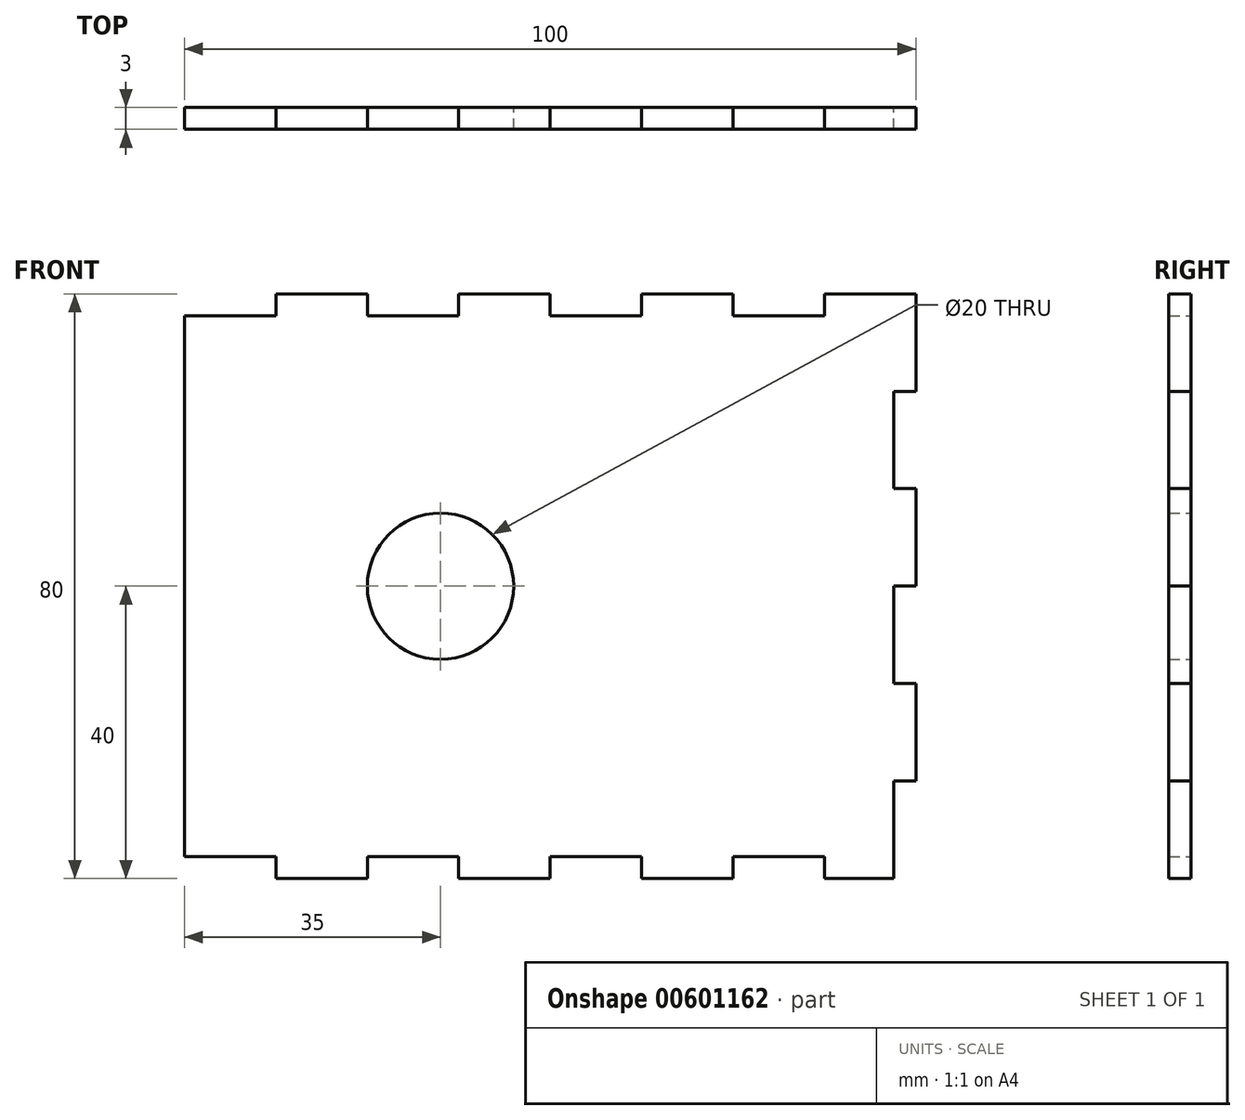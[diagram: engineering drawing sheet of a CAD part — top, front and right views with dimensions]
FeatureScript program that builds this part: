
annotation { "Feature Type Name" : "Feature", "Feature Type Description" : "" }
export const myFeature = defineFeature(function(context is Context, id is Id, definition is map)
    precondition{}
    {
        {
            var Q0;
            Q0=qCreatedBy(makeId("Front.planeOp"),FACE);
            var sketch = newSketch(context, id + "F0", { "sketchPlane" : qUnion([Q0])});
            skLineSegment(sketch, "E0.bottom", {"start": v(47, -40) * mm, "end": v(37.5, -40) * mm});
            skLineSegment(sketch, "E0.left", {"start": v(50, -26.67) * mm, "end": v(50, -13.33) * mm});
            skLineSegment(sketch, "E0.right", {"start": v(-50, -37) * mm, "end": v(-50, 37) * mm});
            skPoint(sketch, "E0.middle", {"position": v(0, 0) * mm});
            skLineSegment(sketch, "E1", {"start": v(-50, -37) * mm, "end": v(-37.5, -37) * mm});
            skLineSegment(sketch, "E2", {"start": v(-37.5, -37) * mm, "end": v(-37.5, -40) * mm});
            skLineSegment(sketch, "E3", {"start": v(-25, -37) * mm, "end": v(-25, -40) * mm});
            skLineSegment(sketch, "E4", {"start": v(-12.5, -37) * mm, "end": v(-12.5, -40) * mm});
            skLineSegment(sketch, "E5", {"start": v(0, -37) * mm, "end": v(0, -40) * mm});
            skLineSegment(sketch, "E6.MirrorCS", {"start": v(37.5, -37) * mm, "end": v(37.5, -40) * mm});
            skLineSegment(sketch, "E7.MirrorCS", {"start": v(25, -37) * mm, "end": v(25, -40) * mm});
            skLineSegment(sketch, "E8.MirrorCS", {"start": v(12.5, -37) * mm, "end": v(12.5, -40) * mm});
            skPoint(sketch, "E9.orphan", {"position": v(-50, -40) * mm});
            skLineSegment(sketch, "E10.trimOffspring", {"start": v(-25, -37) * mm, "end": v(-12.5, -37) * mm});
            skLineSegment(sketch, "E11.trimOffspring", {"start": v(-25, -40) * mm, "end": v(-37.5, -40) * mm});
            skLineSegment(sketch, "E12.trimOffspring", {"start": v(0, -37) * mm, "end": v(12.5, -37) * mm});
            skLineSegment(sketch, "E13.trimOffspring", {"start": v(0, -40) * mm, "end": v(-12.5, -40) * mm});
            skLineSegment(sketch, "E14.trimOffspring", {"start": v(25, -37) * mm, "end": v(37.5, -37) * mm});
            skLineSegment(sketch, "E15.trimOffspring", {"start": v(25, -40) * mm, "end": v(12.5, -40) * mm});
            skLineSegment(sketch, "E16.MirrorCS", {"start": v(0, 37) * mm, "end": v(0, 40) * mm});
            skLineSegment(sketch, "E17.MirrorCS", {"start": v(-37.5, 37) * mm, "end": v(-37.5, 40) * mm});
            skLineSegment(sketch, "E18.MirrorCS", {"start": v(-25, 37) * mm, "end": v(-25, 40) * mm});
            skLineSegment(sketch, "E19.MirrorCS", {"start": v(-12.5, 37) * mm, "end": v(-12.5, 40) * mm});
            skLineSegment(sketch, "E20.MirrorCS", {"start": v(37.5, 37) * mm, "end": v(37.5, 40) * mm});
            skLineSegment(sketch, "E21.MirrorCS", {"start": v(25, 37) * mm, "end": v(25, 40) * mm});
            skLineSegment(sketch, "E22.MirrorCS", {"start": v(12.5, 37) * mm, "end": v(12.5, 40) * mm});
            skPoint(sketch, "E23.MirrorP", {"position": v(-50, 40) * mm});
            skLineSegment(sketch, "E24.MirrorCS", {"start": v(25, 40) * mm, "end": v(12.5, 40) * mm});
            skLineSegment(sketch, "E25.MirrorCS", {"start": v(-25, 40) * mm, "end": v(-37.5, 40) * mm});
            skLineSegment(sketch, "E26.MirrorCS", {"start": v(0, 37) * mm, "end": v(12.5, 37) * mm});
            skLineSegment(sketch, "E27.MirrorCS", {"start": v(0, 40) * mm, "end": v(-12.5, 40) * mm});
            skLineSegment(sketch, "E28.MirrorCS", {"start": v(50, 40) * mm, "end": v(37.5, 40) * mm});
            skLineSegment(sketch, "E29.MirrorCS", {"start": v(-50, 37) * mm, "end": v(-37.5, 37) * mm});
            skLineSegment(sketch, "E30.MirrorCS", {"start": v(-25, 37) * mm, "end": v(-12.5, 37) * mm});
            skLineSegment(sketch, "E31.MirrorCS", {"start": v(25, 37) * mm, "end": v(37.5, 37) * mm});
            skCircle(sketch, "E32", {"center": v(-15, 0) * mm, "radius": 10 * mm});
            skLineSegment(sketch, "E33", {"start": v(47, 26.67) * mm, "end": v(47, 13.33) * mm});
            skLineSegment(sketch, "E34", {"start": v(47, 26.67) * mm, "end": v(50, 26.67) * mm});
            skLineSegment(sketch, "E35", {"start": v(47, 13.33) * mm, "end": v(50, 13.33) * mm});
            skLineSegment(sketch, "E36", {"start": v(47, 0) * mm, "end": v(50, 0) * mm});
            skLineSegment(sketch, "E37", {"start": v(47, -13.33) * mm, "end": v(50, -13.33) * mm});
            skLineSegment(sketch, "E38", {"start": v(47, -26.67) * mm, "end": v(50, -26.67) * mm});
            skLineSegment(sketch, "E39.trimOffspring", {"start": v(50, 26.67) * mm, "end": v(50, 40) * mm});
            skLineSegment(sketch, "E40.trimOffspring", {"start": v(47, 0) * mm, "end": v(47, -13.33) * mm});
            skLineSegment(sketch, "E41.trimOffspring", {"start": v(50, 0) * mm, "end": v(50, 13.33) * mm});
            skLineSegment(sketch, "E42.trimOffspring", {"start": v(47, -26.67) * mm, "end": v(47, -40) * mm});
            skPoint(sketch, "E43.orphan", {"position": v(50, -40) * mm});
            skSolve(sketch);
        }
        {
            var Q0;
            Q0=makeQuery(id+"F0.imprint","IMPRINT",FACE,{"disambiguationData":[TD([[makeQuery(id+"F0.imprint","IMPRINT",EDGE,{"derivedFrom":sQuery(id+"F0.wireOp",EDGE,"E0.bottom")}),-1.0]])]});
            extrude(context, id + "F1", {"entities" : qUnion([Q0]), "depth" : 3 * mm, "offsetDistance" : 25 * mm});
        }
    });
